# Revit family: E-702_RFA
name_source: partatom
category: Aparatos sanitarios
units: mm (PartAtom-declared; Revit-internal decimal feet)

## family parameters
Compartido = No
Corte con vacíos al cargar = No
Cota de conector redondo = Diámetro de uso
Número OmniClass = 23.45.00.00
Punto de cálculo de habitación = No
Se basa en plano de trabajo = No
Siempre vertical = Sí
Tipo de pieza = Normal
Título OmniClass = Sanitary, Laundry, and Cleaning Equipment

## types (1)
- E-702
    Brass Chromed = Brass
    Comentarios de tipo = Shower, Tub Or Hand Shower Single Control Faucet
    Data Sheet = https://helvex.com.mx
    Descripción = Premier Single Control For Shower Or Tub
    Elevación por defecto = 0"
    Fabricante = HELVEX
    Features = Ceramic Cartridge; Includes Setting Tools For Installation And Maintenance
    Inlet Threads = ½" - 14 NPT
    Installation Adjustment = 1" (25.4 mm) Max.
    Instructive = https://helvex.com.mx
    Max. Working Pressure = 85.3 psi
    Min. Working Pressure = 14.2 psi
    Modelo = E-702
    Satin = Satín
    Total Height = 2"
    Total Length = 7"
    Total Width = 4"
    URL = https://helvex.com.mx

## geometry (parser evidence)
native form markers: Sweep x3
no freeform markers — native parametric forms only
